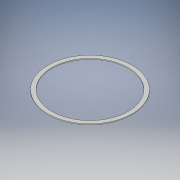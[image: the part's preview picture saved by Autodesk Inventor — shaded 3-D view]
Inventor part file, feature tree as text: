
AUTODESK INVENTOR PART (.ipt)
format: ipt  version: 2017 (Build 210142000, 142)  size: 101,888 bytes
history: native  units: in
note: dims shown in document units (in); Inventor stores cm internally (conversion verified against a paired STEP export)
features: extrude x2, sketch x2
ambient origin geometry x8: Origin, YZ Plane, XZ Plane, XY Plane, X Axis, Y Axis, Z Axis, Center Point
bodies: Solid1 (feature_tree)
feature tree (4):
  extrude  "Extrusion1"  Depth=0.125in TaperAngle=0.0deg
  extrude  "Extrusion2"  Depth=0.125in TaperAngle=0.0deg
  sketch  "Sketch1"  dims[d0=12.0in d1=0.125in d2=0.0in]
  sketch  "Sketch2"  dims[d3=10.875in d4=0.125in d5=0.0in]
